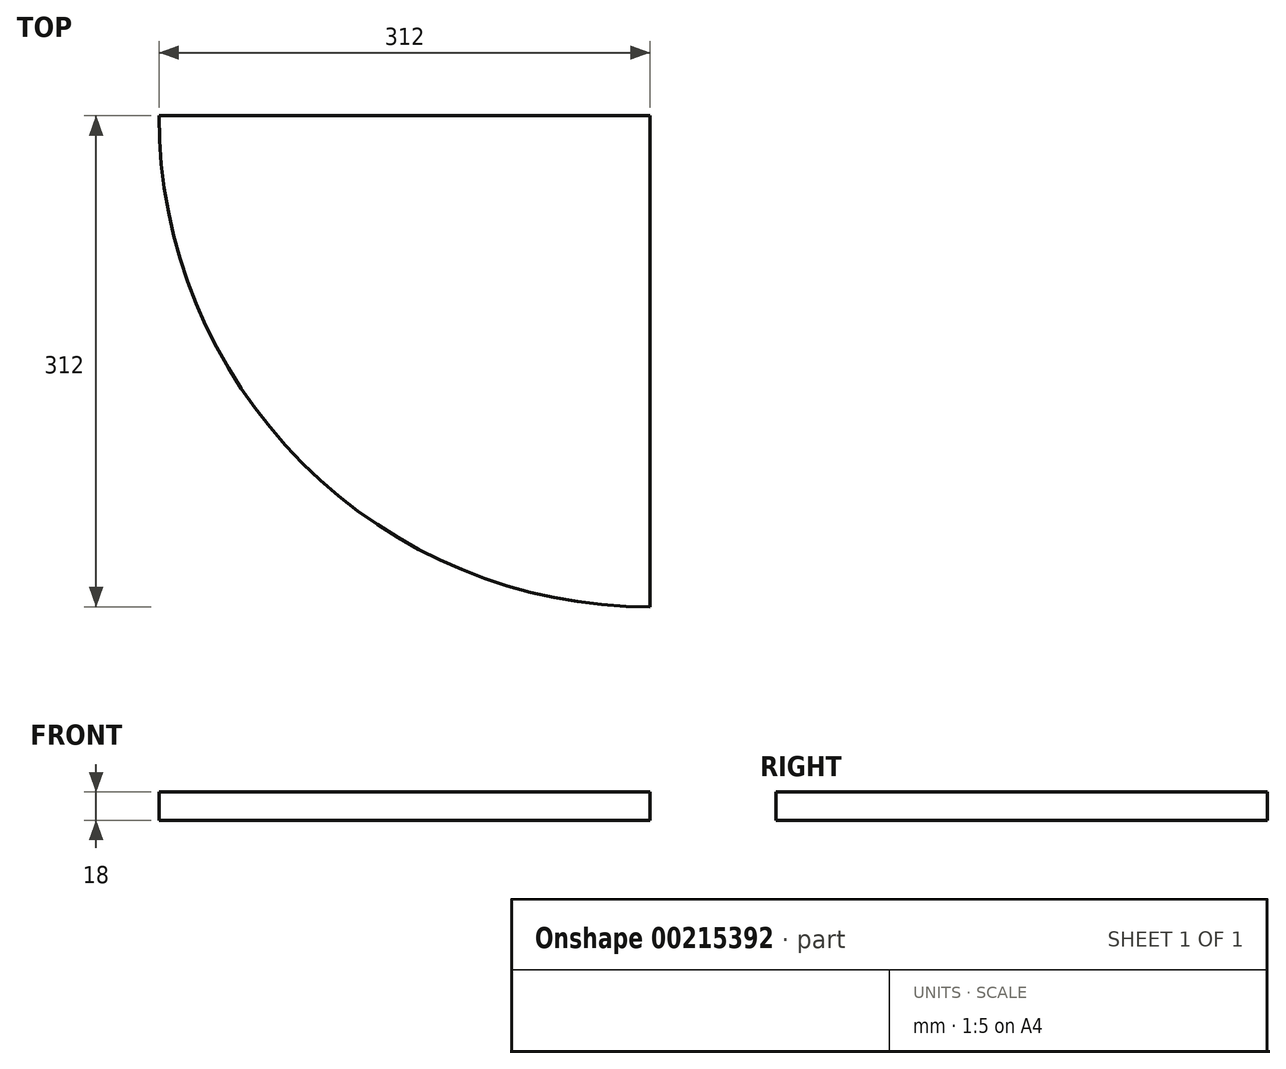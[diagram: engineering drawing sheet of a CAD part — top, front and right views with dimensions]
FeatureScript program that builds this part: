
annotation { "Feature Type Name" : "Feature", "Feature Type Description" : "" }
export const myFeature = defineFeature(function(context is Context, id is Id, definition is map)
    precondition{}
    {
        {
            var Q0;
            Q0=qCreatedBy(makeId("Top.planeOp"),FACE);
            var sketch = newSketch(context, id + "F0", { "sketchPlane" : qUnion([Q0])});
            skLineSegment(sketch, "E0", {"start": v(0, 0) * mm, "end": v(0, 312) * mm});
            skLineSegment(sketch, "E1", {"start": v(0, 312) * mm, "end": v(-312, 312) * mm});
            skArc(sketch, "E2", {"start": v(-312, 312) * mm, "mid": v(-220.77, 91.23) * mm, "end": v(0, 0) * mm});
            skSolve(sketch);
        }
        {
            var Q0;
            Q0=qSketchRegion(id+"F0",true);
            extrude(context, id + "F1", {"entities" : qUnion([Q0]), "depth" : 18 * mm});
        }
    });
